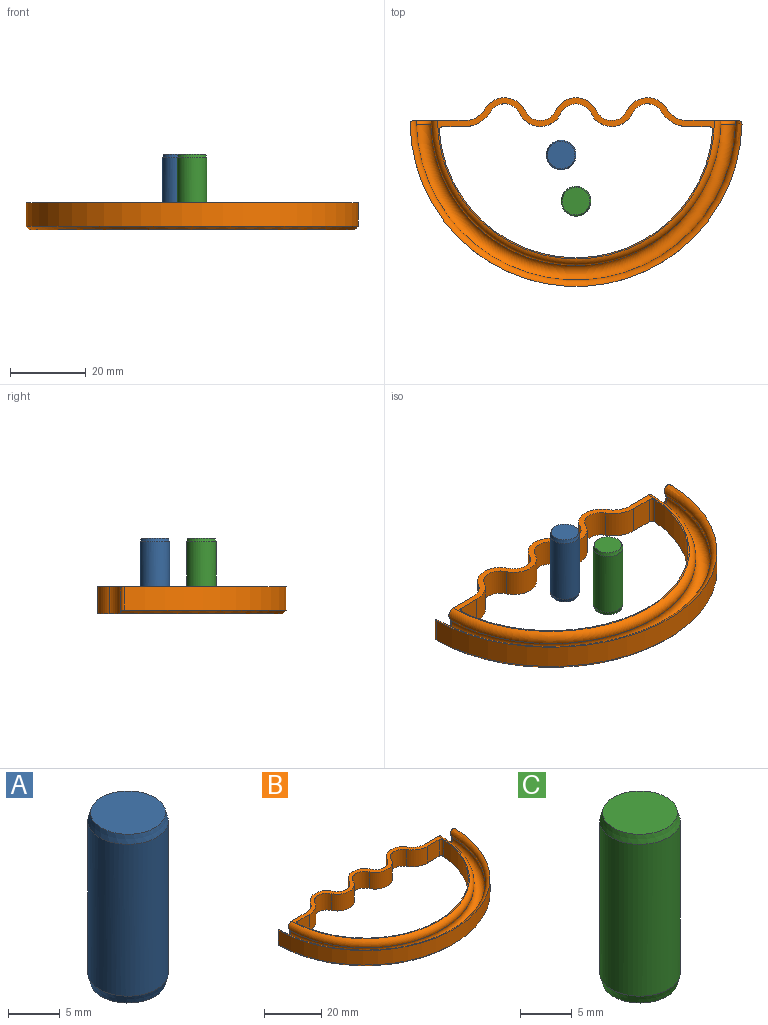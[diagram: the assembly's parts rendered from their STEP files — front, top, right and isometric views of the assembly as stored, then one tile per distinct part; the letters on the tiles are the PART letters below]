
ASSEMBLY  parts=3 mates=2
PART A: 5 faces, bbox 7.8x7.8x20 mm
  f0: cylinder r=3.9mm len=18mm, axis (0,0,1), area 441.1mm2, adj f1,f4
  f1: cone r=3.9mm half-angle=15deg, axis (0,0,-1), area 24.5mm2, adj f0,f3
  f2: plane 7.26x7.26mm, normal (0,0,-1), area 41.4mm2, adj f4
  f3: plane 7.26x7.26mm, normal (0,0,1), area 41.4mm2, adj f1
  f4: cone r=3.9mm half-angle=15deg, axis (0,0,1), area 24.5mm2, adj f0,f2
PART B: 34 faces, bbox 95.9x54x7.3 mm
  f0: torus R=44.31mm, axis (0,0,-1), area 490.3mm2, adj f1,f4,f5,f6,f7,f14,f22,f25
  f1: bspline ~6.4x5.58mm, area 17.5mm2, adj f0,f5,f15,f22,f24,f25
  f2: cone r=43.8mm half-angle=45deg, axis (0,0,1), area 190.9mm2, adj f3,f4,f5,f6
  f3: plane 85.6x48.8mm, normal (0,0,-1), area 957.4mm2, adj f2,f5,f6,f9,f10,f11,f12,f13
  f4: cylinder r=43.8mm len=87.58mm, axis (0,0,1), area 840.4mm2, adj f0,f2,f5,f6
  f5: cylinder r=1mm len=7.2mm, axis (0,0,1), area 9.5mm2, adj f0,f1,f2,f3,f4,f22,f24
  f6: cylinder r=1mm len=7.2mm, axis (0,0,1), area 9.5mm2, adj f0,f2,f3,f4,f7,f14,f23
  f7: bspline ~6.4x5.64mm, area 17.5mm2, adj f0,f6,f14,f15,f23,f25
  f8: plane 73.04x42.52mm, normal (0,0,1), area 174.9mm2, adj f9,f10,f11,f12,f13,f15,f16,f17
  f9: plane 7.2x5.86mm, normal (0,-1,0), area 42.2mm2, adj f3,f8,f12,f33
  f10: plane 7.2x5.86mm, normal (0,-1,0), area 42.2mm2, adj f3,f8,f13,f21
  f11: cylinder r=36.2mm len=72.2mm, axis (0,0,1), area 780.3mm2, adj f3,f8,f12,f13
  f12: cylinder r=1mm len=7.2mm, axis (0,0,1), area 11.8mm2, adj f3,f8,f9,f11
  f13: cylinder r=1mm len=7.2mm, axis (0,0,1), area 11.8mm2, adj f3,f8,f10,f11
  f14: plane 1.24x0.48mm, normal (0,1,0), area 0.3mm2, adj f0,f6,f7
  f15: torus R=36.01mm, axis (0,0,-1), area 434.9mm2, adj f1,f7,f8,f23,f24,f25
  f16: cylinder r=6mm len=7.2mm, axis (0,0,1), area 45.2mm2, adj f3,f8,f17,f24
  f17: cylinder r=6mm len=10.63mm, axis (0,0,1), area 94.2mm2, adj f3,f8,f16,f18
  f18: cylinder r=4.4mm len=7.97mm, axis (0,0,1), area 71.8mm2, adj f3,f8,f17,f29
  f19: cylinder r=6mm len=10.87mm, axis (0,0,1), area 98mm2, adj f3,f8,f20,f28
  f20: cylinder r=4.4mm len=7.8mm, axis (0,0,1), area 69.1mm2, adj f3,f8,f19,f21
  f21: cylinder r=7.6mm len=7.2mm, axis (0,0,1), area 57.3mm2, adj f3,f8,f10,f20
  f22: plane 1.24x0.49mm, normal (0,1,0), area 0.3mm2, adj f0,f1,f5
  f23: plane 13.56x7.21mm, normal (0,1,0), area 62.6mm2, adj f3,f6,f7,f8,f15,f32
  f24: plane 13.55x7.2mm, normal (0,1,0), area 62.6mm2, adj f1,f3,f5,f8,f15,f16
  f25: torus R=40.16mm, axis (0,0,-1), area 1043mm2, adj f0,f1,f7,f15
  f26: cylinder r=6mm len=10.87mm, axis (0,0,1), area 98mm2, adj f3,f8,f27,f28
  f27: cylinder r=4.4mm len=7.8mm, axis (0,0,1), area 69.1mm2, adj f3,f8,f26,f33
  f28: cylinder r=4.4mm len=7.97mm, axis (0,0,1), area 71.8mm2, adj f3,f8,f19,f26
  f29: cylinder r=6mm len=10.87mm, axis (0,0,1), area 98mm2, adj f3,f8,f18,f30
  f30: cylinder r=4.4mm len=7.97mm, axis (0,0,1), area 71.8mm2, adj f3,f8,f29,f31
  f31: cylinder r=6mm len=10.63mm, axis (0,0,1), area 94.2mm2, adj f3,f8,f30,f32
  f32: cylinder r=6mm len=7.2mm, axis (0,0,1), area 45.2mm2, adj f3,f8,f23,f31
  f33: cylinder r=7.6mm len=7.2mm, axis (0,0,1), area 57.3mm2, adj f3,f8,f9,f27
PART C: 5 faces, bbox 7.8x7.8x20 mm
  f0: cone r=3.9mm half-angle=15deg, axis (0,0,1), area 24.5mm2, adj f3,f4
  f1: cone r=3.9mm half-angle=15deg, axis (0,0,-1), area 24.5mm2, adj f2,f4
  f2: plane 7.26x7.26mm, normal (0,0,1), area 41.4mm2, adj f1
  f3: plane 7.26x7.26mm, normal (0,0,-1), area 41.4mm2, adj f0
  f4: cylinder r=3.9mm len=18mm, axis (0,0,1), area 441.1mm2, adj f0,f1
PLACE A t=(-46.27,-4.12,-3.51)mm
PLACE B t=(-27.06,115.01,-9.91)mm
PLACE C t=(-11.76,-16.31,-3.51)mm
MATE parallel C.f0 <-> B.f3  axis (0,0,-1) through (-27.06,-16.31,-3.51)mm
MATE parallel B.f3 <-> A.f0  axis (0,0,-1) through (-27.06,-16.31,-3.51)mm
